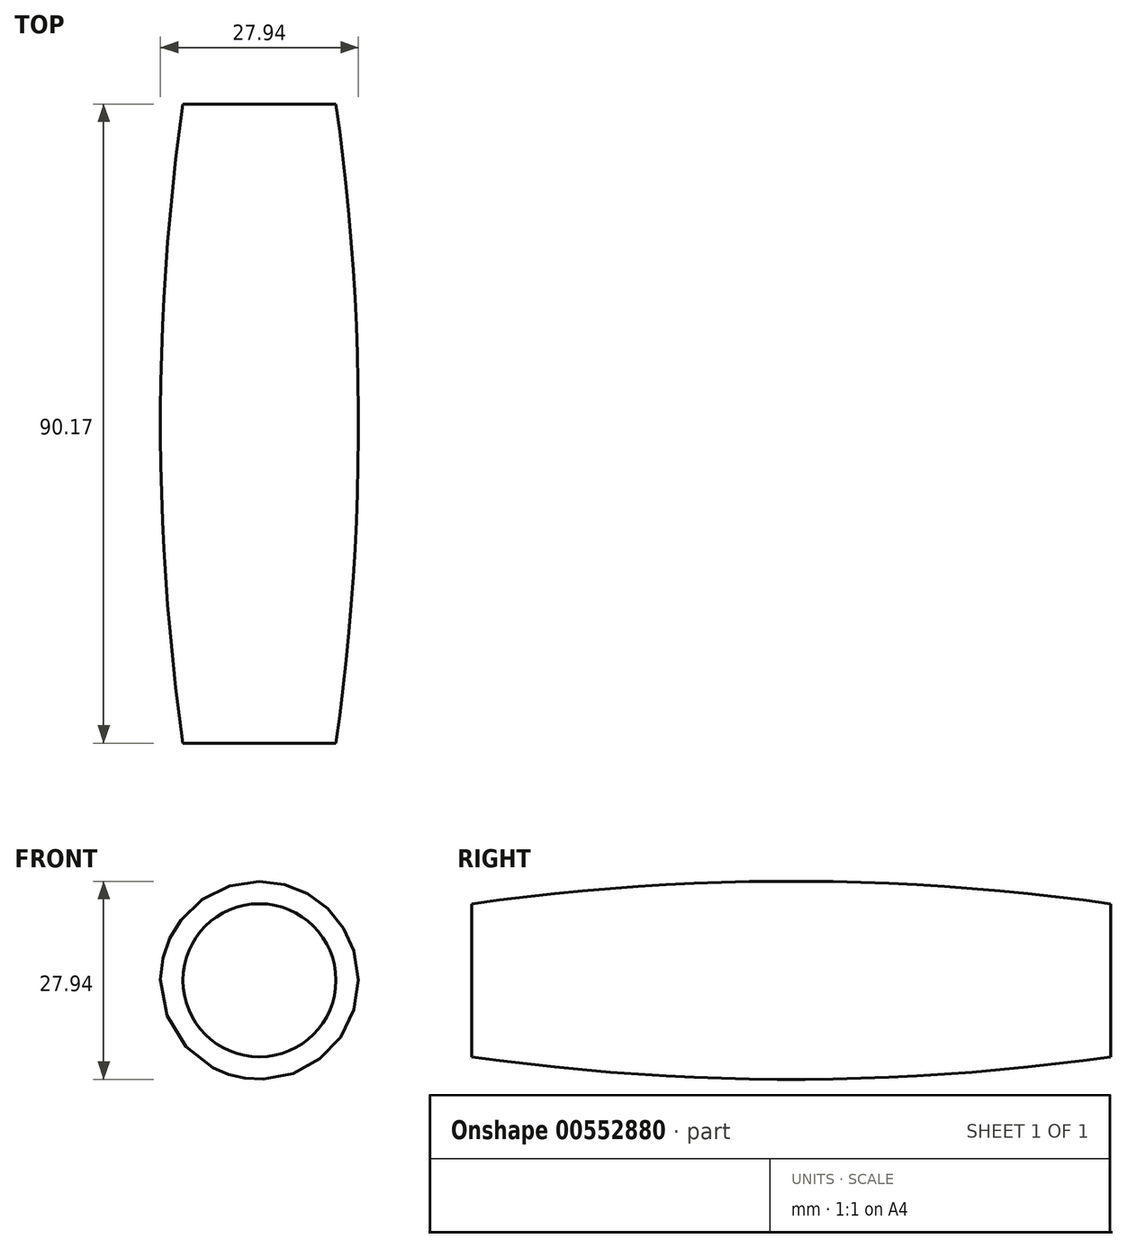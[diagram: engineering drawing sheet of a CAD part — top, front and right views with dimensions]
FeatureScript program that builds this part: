
annotation { "Feature Type Name" : "Feature", "Feature Type Description" : "" }
export const myFeature = defineFeature(function(context is Context, id is Id, definition is map)
    precondition{}
    {
        {
            var Q0;
            Q0=qCreatedBy(makeId("Top.planeOp"),FACE);
            var sketch = newSketch(context, id + "F0", { "sketchPlane" : qUnion([Q0])});
            skLineSegment(sketch, "E0", {"start": v(0, 0) * mm, "end": v(0, -90.17) * mm});
            skLineSegment(sketch, "E1", {"start": v(0, -90.17) * mm, "end": v(10.8, -90.17) * mm});
            skLineSegment(sketch, "E2", {"start": v(0, 0) * mm, "end": v(10.8, 0) * mm});
            skArc(sketch, "E3", {"start": v(10.8, -90.17) * mm, "mid": v(13.97, -45.09) * mm, "end": v(10.8, 0) * mm});
            skSolve(sketch);
        }
        {
            var Q0;
            Q0=makeQuery(id+"F0.imprint","IMPRINT",FACE,{"disambiguationData":[TD([[makeQuery(id+"F0.imprint","IMPRINT",EDGE,{"derivedFrom":sQuery(id+"F0.wireOp",EDGE,"E0")}),1.0]])]});
            var Q1;
            Q1=sQuery(id+"F0.wireOp",EDGE,"E0");
            revolve(context, id + "F1", {"entities" : qUnion([Q0]), "axis" : qUnion([Q1]), "revolveType" : RevolveType.FULL});
        }
    });
